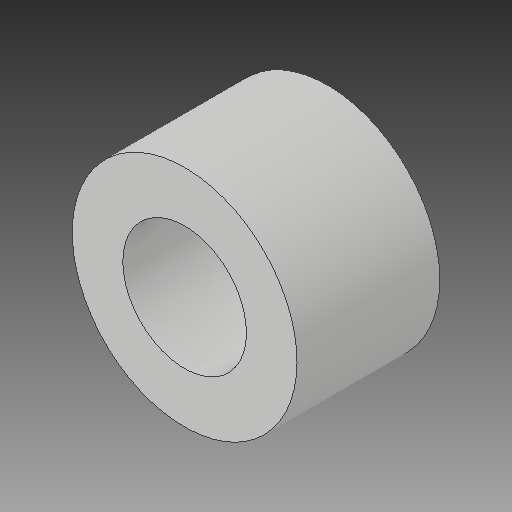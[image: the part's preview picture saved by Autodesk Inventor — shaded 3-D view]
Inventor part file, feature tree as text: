
AUTODESK INVENTOR PART (.ipt)
format: ipt  version: 2017 (Build 210142000, 142)  size: 100,864 bytes
history: native  units: mm
features: other x3, sketch x1
ambient origin geometry x8: Origin, YZ Plane, XZ Plane, XY Plane, X Axis, Y Axis, Z Axis, Center Point
bodies: Solid1 (feature_tree)
feature tree (4):
  other  "Small-Aluminium-Spacer.ipt"
  other  "Solid1::Small-Aluminium-Spacer.ipt"
  other  "TaggingFeature1"
  sketch  "Sketch1"  dims[d0=10.0mm]
